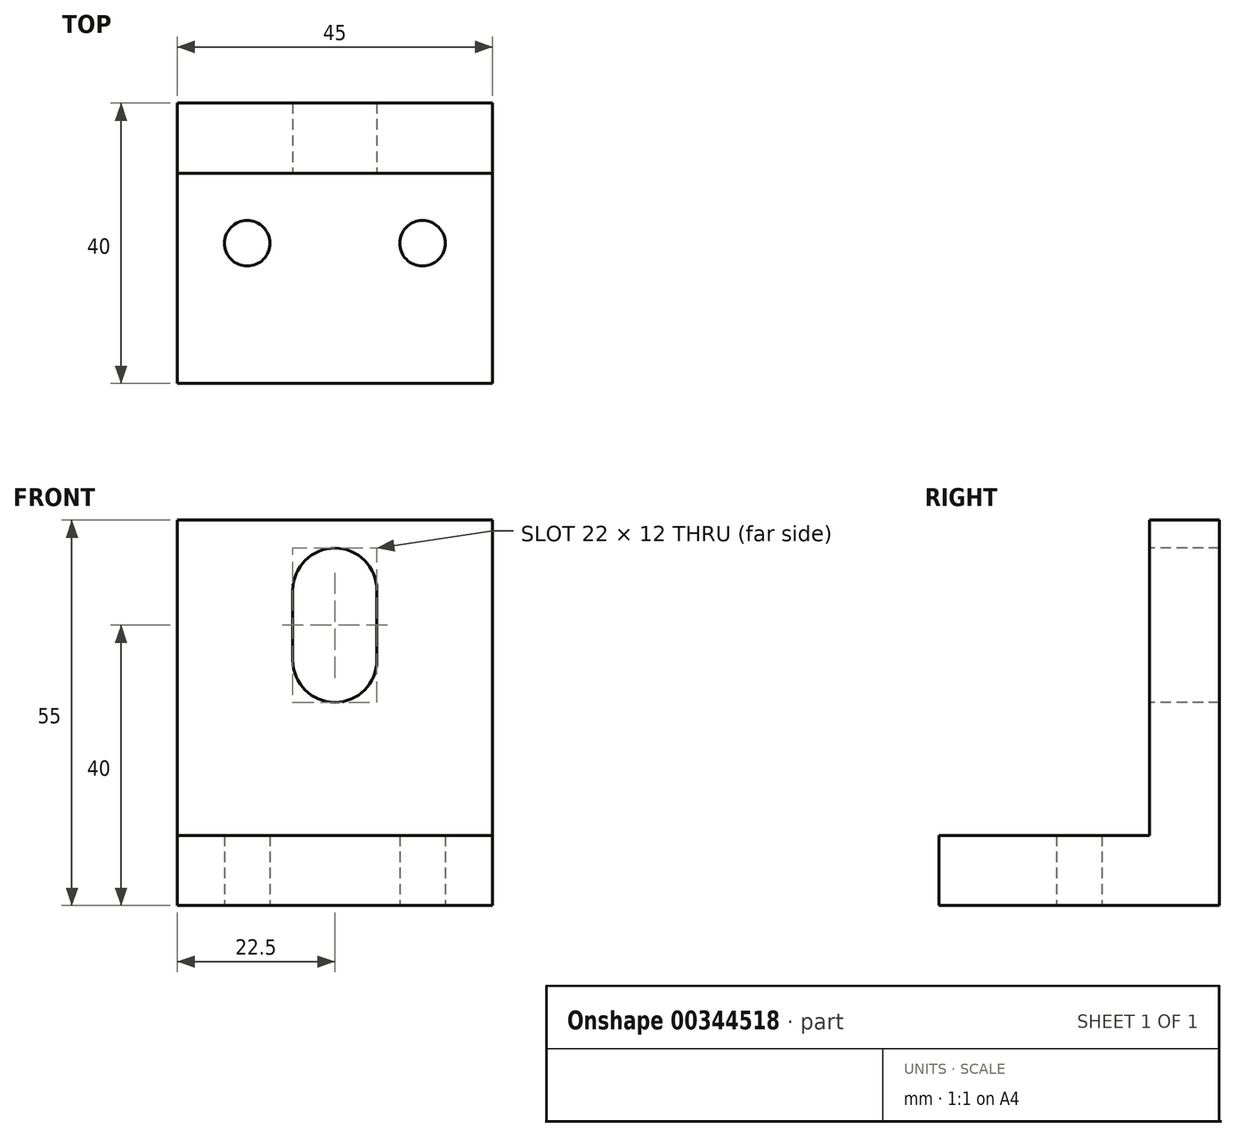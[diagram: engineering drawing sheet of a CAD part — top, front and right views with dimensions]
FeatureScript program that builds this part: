
annotation { "Feature Type Name" : "Feature", "Feature Type Description" : "" }
export const myFeature = defineFeature(function(context is Context, id is Id, definition is map)
    precondition{}
    {
        {
            var Q0;
            Q0=qCreatedBy(makeId("Front.planeOp"),FACE);
            var sketch = newSketch(context, id + "F0", { "sketchPlane" : qUnion([Q0])});
            skLineSegment(sketch, "E0.bottom", {"start": v(22.5, -27.5) * mm, "end": v(-22.5, -27.5) * mm});
            skLineSegment(sketch, "E0.top", {"start": v(22.5, 27.5) * mm, "end": v(-22.5, 27.5) * mm});
            skLineSegment(sketch, "E0.left", {"start": v(22.5, -27.5) * mm, "end": v(22.5, 27.5) * mm});
            skLineSegment(sketch, "E0.right", {"start": v(-22.5, -27.5) * mm, "end": v(-22.5, 27.5) * mm});
            skPoint(sketch, "E0.middle", {"position": v(0, 0) * mm});
            skSolve(sketch);
        }
        {
            var Q0;
            Q0=makeQuery(id+"F0.imprint","IMPRINT",FACE,{"disambiguationData":[TD([[makeQuery(id+"F0.imprint","IMPRINT",EDGE,{"derivedFrom":sQuery(id+"F0.wireOp",EDGE,"E0.bottom")}),-1.0]])]});
            extrude(context, id + "F1", {"entities" : qUnion([Q0]), "depth" : 10 * mm});
        }
        {
            var Q0;
            Q0=makeQuery(id+"F1.opExtrude","CAP_FACE",FACE,{"disambiguationData":[OSD([sQuery(id+"F0.wireOp",EDGE,"E0.bottom"),sQuery(id+"F0.wireOp",EDGE,"E0.top"),sQuery(id+"F0.wireOp",EDGE,"E0.left"),sQuery(id+"F0.wireOp",EDGE,"E0.right")])],"isStart":false});
            var sketch = newSketch(context, id + "F2", { "sketchPlane" : qUnion([Q0])});
            skLineSegment(sketch, "E1.bottom", {"start": v(22.5, -27.5) * mm, "end": v(-22.5, -27.5) * mm});
            skLineSegment(sketch, "E1.top", {"start": v(22.5, -17.5) * mm, "end": v(-22.5, -17.5) * mm});
            skLineSegment(sketch, "E1.left", {"start": v(22.5, -27.5) * mm, "end": v(22.5, -17.5) * mm});
            skLineSegment(sketch, "E1.right", {"start": v(-22.5, -27.5) * mm, "end": v(-22.5, -17.5) * mm});
            skSolve(sketch);
        }
        {
            var Q0;
            Q0=makeQuery(id+"F2.imprint","IMPRINT",FACE,{"disambiguationData":[TD([[makeQuery(id+"F2.imprint","IMPRINT",EDGE,{"derivedFrom":sQuery(id+"F2.wireOp",EDGE,"E1.bottom")}),-1.0]])]});
            extrude(context, id + "F3", {"entities" : qUnion([Q0]), "operationType" : NewBodyOperationType.ADD, "depth" : 30 * mm});
        }
        {
            var Q0;
            Q0=makeQuery(id+"F1.opExtrude","CAP_FACE",FACE,{"disambiguationData":[OSD([sQuery(id+"F0.wireOp",EDGE,"E0.bottom"),sQuery(id+"F0.wireOp",EDGE,"E0.top"),sQuery(id+"F0.wireOp",EDGE,"E0.left"),sQuery(id+"F0.wireOp",EDGE,"E0.right")])],"isStart":false});
            var sketch = newSketch(context, id + "F4", { "sketchPlane" : qUnion([Q0])});
            skLineSegment(sketch, "E2.bottom", {"start": v(6, 7.5) * mm, "end": v(-6, 7.5) * mm});
            skLineSegment(sketch, "E2.top", {"start": v(6, 17.5) * mm, "end": v(-6, 17.5) * mm});
            skLineSegment(sketch, "E2.left", {"start": v(6, 7.5) * mm, "end": v(6, 17.5) * mm});
            skLineSegment(sketch, "E2.right", {"start": v(-6, 7.5) * mm, "end": v(-6, 17.5) * mm});
            skPoint(sketch, "E2.middle", {"position": v(0, 12.5) * mm});
            skPoint(sketch, "E3", {"position": v(0, 17.5) * mm});
            skPoint(sketch, "E4", {"position": v(0, 7.5) * mm});
            skSolve(sketch);
        }
        {
            var Q0;
            Q0=makeQuery(id+"F4.imprint","IMPRINT",FACE,{"disambiguationData":[TD([[makeQuery(id+"F4.imprint","IMPRINT",EDGE,{"derivedFrom":sQuery(id+"F4.wireOp",EDGE,"E2.bottom")}),-1.0]])]});
            extrude(context, id + "F5", {"entities" : qUnion([Q0]), "operationType" : NewBodyOperationType.REMOVE, "oppositeDirection" : true, "depth" : 10 * mm});
        }
        {
            var Q0;
            Q0=makeQuery(id+"F1.opExtrude","CAP_FACE",FACE,{"disambiguationData":[OSD([sQuery(id+"F0.wireOp",EDGE,"E0.bottom"),sQuery(id+"F0.wireOp",EDGE,"E0.top"),sQuery(id+"F0.wireOp",EDGE,"E0.left"),sQuery(id+"F0.wireOp",EDGE,"E0.right")])],"isStart":false});
            var sketch = newSketch(context, id + "F6", { "sketchPlane" : qUnion([Q0])});
            skPoint(sketch, "E5", {"position": v(0, 17.5) * mm});
            skPoint(sketch, "E6", {"position": v(0, 7.5) * mm});
            skSolve(sketch);
        }
        {
            var Q0;
            Q0=sQuery(id+"F6.wireOp",VERTEX,"E5");
            var Q1;
            Q1=sQuery(id+"F6.wireOp",VERTEX,"E6");
            var Q2;
            Q2=makeQuery(id+"F1.opExtrude","SWEPT_BODY",BODY,{"disambiguationData":[OSD([sQuery(id+"F0.wireOp",EDGE,"E0.bottom"),sQuery(id+"F0.wireOp",EDGE,"E0.top"),sQuery(id+"F0.wireOp",EDGE,"E0.left"),sQuery(id+"F0.wireOp",EDGE,"E0.right")])]});
            hole(context, id + "F7", {"style" : HoleStyle.SIMPLE, "endStyle" : HoleEndStyle.BLIND, "holeDiameter" : 12 * mm, "holeDepth" : 16 * mm, "isTappedThrough" : true, "tappedDepth" : 12 * mm, "tapClearance" : 3, "locations" : qUnion([Q0, Q1]), "scope" : qUnion([Q2])});
        }
        {
            var Q0;
            Q0=makeQuery(id+"F3.boolean.opBoolean","MERGE",FACE,{"derivedFrom":[makeQuery(id+"F1.opExtrude","SWEPT_FACE",FACE,{"disambiguationData":[OSD([sQuery(id+"F0.wireOp",EDGE,"E0.bottom")])]}),makeQuery(id+"F3.opExtrude","SWEPT_FACE",FACE,{"disambiguationData":[OSD([sQuery(id+"F2.wireOp",EDGE,"E1.bottom")])]})]});
            var sketch = newSketch(context, id + "F8", { "sketchPlane" : qUnion([Q0])});
            skPoint(sketch, "E7", {"position": v(-12.5, 20) * mm});
            skPoint(sketch, "E8.MirrorP", {"position": v(12.5, 20) * mm});
            skSolve(sketch);
        }
        {
            var Q0;
            Q0=sQuery(id+"F8.wireOp",VERTEX,"E7");
            var Q1;
            Q1=sQuery(id+"F8.wireOp",VERTEX,"E8.MirrorP");
            var Q2;
            Q2=makeQuery(id+"F1.opExtrude","SWEPT_BODY",BODY,{"disambiguationData":[OSD([sQuery(id+"F0.wireOp",EDGE,"E0.bottom"),sQuery(id+"F0.wireOp",EDGE,"E0.top"),sQuery(id+"F0.wireOp",EDGE,"E0.left"),sQuery(id+"F0.wireOp",EDGE,"E0.right")])]});
            hole(context, id + "F9", {"style" : HoleStyle.SIMPLE, "endStyle" : HoleEndStyle.BLIND, "holeDiameter" : 6.5 * mm, "holeDepth" : 10 * mm, "isTappedThrough" : true, "tappedDepth" : 12 * mm, "tapClearance" : 3, "locations" : qUnion([Q0, Q1]), "scope" : qUnion([Q2])});
        }
    });
